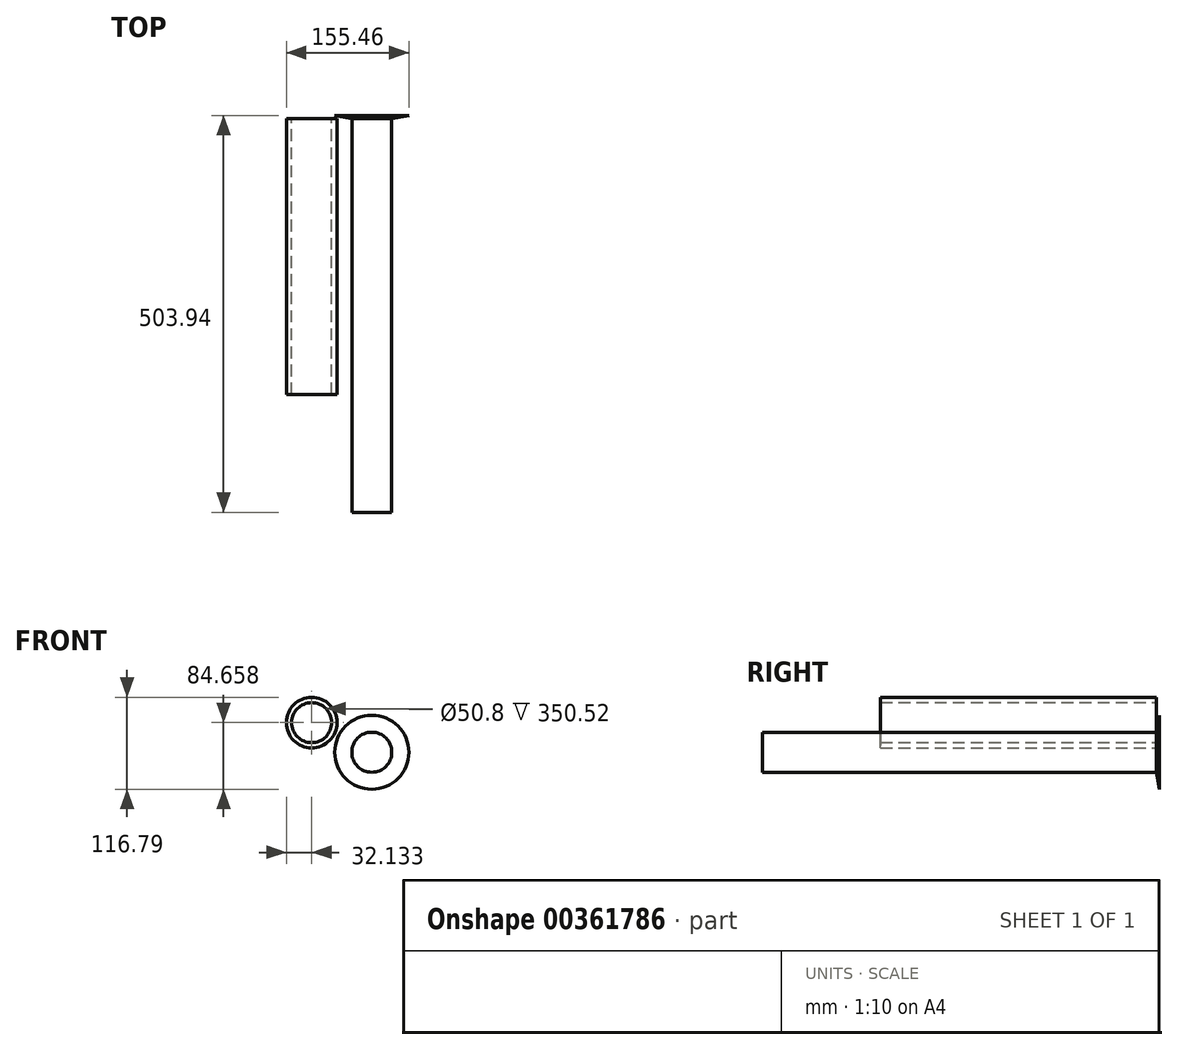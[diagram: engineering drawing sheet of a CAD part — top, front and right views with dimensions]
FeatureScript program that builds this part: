
annotation { "Feature Type Name" : "Feature", "Feature Type Description" : "" }
export const myFeature = defineFeature(function(context is Context, id is Id, definition is map)
    precondition{}
    {
        {
            var Q0;
            Q0=qCreatedBy(makeId("Front.planeOp"),FACE);
            var sketch = newSketch(context, id + "F0", { "sketchPlane" : qUnion([Q0])});
            skCircle(sketch, "E0", {"center": v(-43.76, 20.99) * mm, "radius": 25.4 * mm});
            skCircle(sketch, "E1", {"center": v(-43.76, 20.99) * mm, "radius": 32.13 * mm});
            skCircle(sketch, "E2", {"center": v(32.56, -16.66) * mm, "radius": 25.4 * mm});
            skSolve(sketch);
        }
        {
            var Q0;
            Q0=makeQuery(id+"F0.imprint","IMPRINT",FACE,{"disambiguationData":[TD([[makeQuery(id+"F0.imprint","IMPRINT",EDGE,{"derivedFrom":sQuery(id+"F0.wireOp",EDGE,"E0")}),-1.0]])]});
            extrude(context, id + "F1", {"entities" : qUnion([Q0]), "depth" : 350.52 * mm});
        }
        {
            var Q0;
            Q0=makeQuery(id+"F0.imprint","IMPRINT",FACE,{"disambiguationData":[TD([[makeQuery(id+"F0.imprint","IMPRINT",EDGE,{"derivedFrom":sQuery(id+"F0.wireOp",EDGE,"E2")}),1.0]])]});
            extrude(context, id + "F2", {"entities" : qUnion([Q0]), "depth" : 500.13 * mm});
        }
        {
            var Q0;
            Q0=makeQuery(id+"F0.imprint","IMPRINT",FACE,{"disambiguationData":[TD([[makeQuery(id+"F0.imprint","IMPRINT",EDGE,{"derivedFrom":sQuery(id+"F0.wireOp",EDGE,"E2")}),1.0]])]});
            var Q1;
            Q1=sQuery(id+"F0.wireOp",EDGE,"E2");
            extrude(context, id + "F3", {"entities" : qUnion([Q0]), "surfaceEntities" : qUnion([Q1]), "oppositeDirection" : true, "depth" : 3.8 * mm, "hasDraft" : true, "draftAngle" : 80 * degree});
        }
    });
